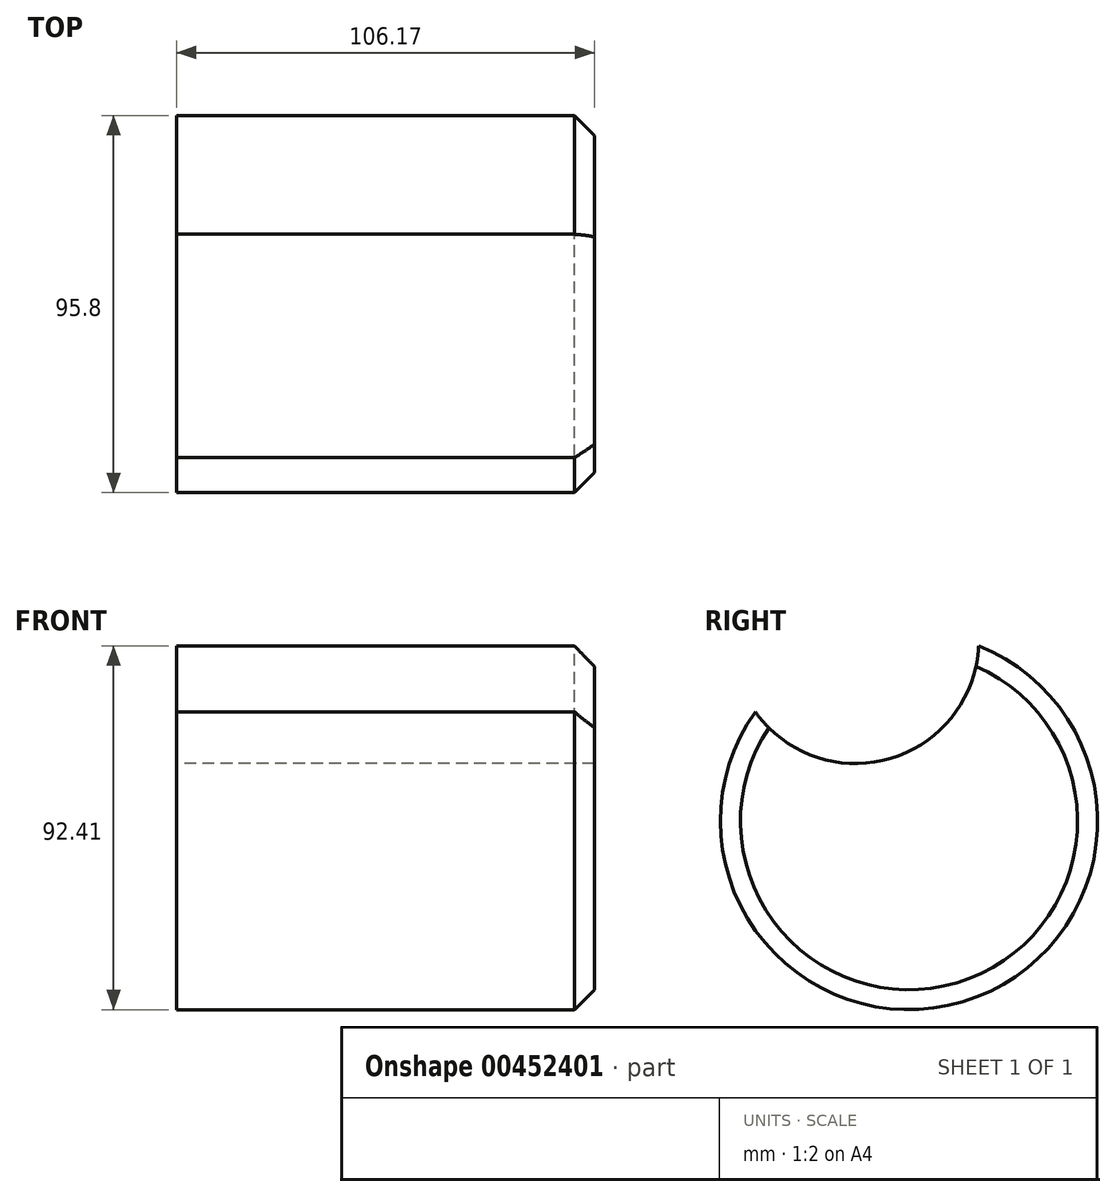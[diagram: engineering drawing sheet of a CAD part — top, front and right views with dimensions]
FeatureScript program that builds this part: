
annotation { "Feature Type Name" : "Feature", "Feature Type Description" : "" }
export const myFeature = defineFeature(function(context is Context, id is Id, definition is map)
    precondition{}
    {
        {
            var Q0;
            Q0=qCreatedBy(makeId("Right.planeOp"),FACE);
            var sketch = newSketch(context, id + "F0", { "sketchPlane" : qUnion([Q0])});
            skArc(sketch, "E0", {"start": v(-39.04, 27.75) * mm, "mid": v(13.57, -45.94) * mm, "end": v(17.69, 44.51) * mm});
            skArc(sketch, "E1", {"start": v(-39.04, 27.75) * mm, "mid": v(-4.7, 15.92) * mm, "end": v(17.69, 44.51) * mm});
            skSolve(sketch);
        }
        {
            var Q0;
            Q0 = qSketchRegion(id + "F0", true);
            extrude(context, id + "F1", {"entities" : qUnion([Q0]), "depth" : 106.17 * mm});
        }
        {
            var Q0;
            Q0=makeQuery(id+"F1.opExtrude","CAP_EDGE",EDGE,{"disambiguationData":[OSD([sQuery(id+"F0.wireOp",EDGE,"E0")])],"isStart":false});
            chamfer(context, id + "F2", {"entities" : qUnion([Q0]), "chamferType" : ChamferType.TWO_OFFSETS, "width1" : 5.08 * mm, "oppositeDirection" : false, "width2" : 5.08 * mm, "tangentPropagation" : true});
        }
    });
